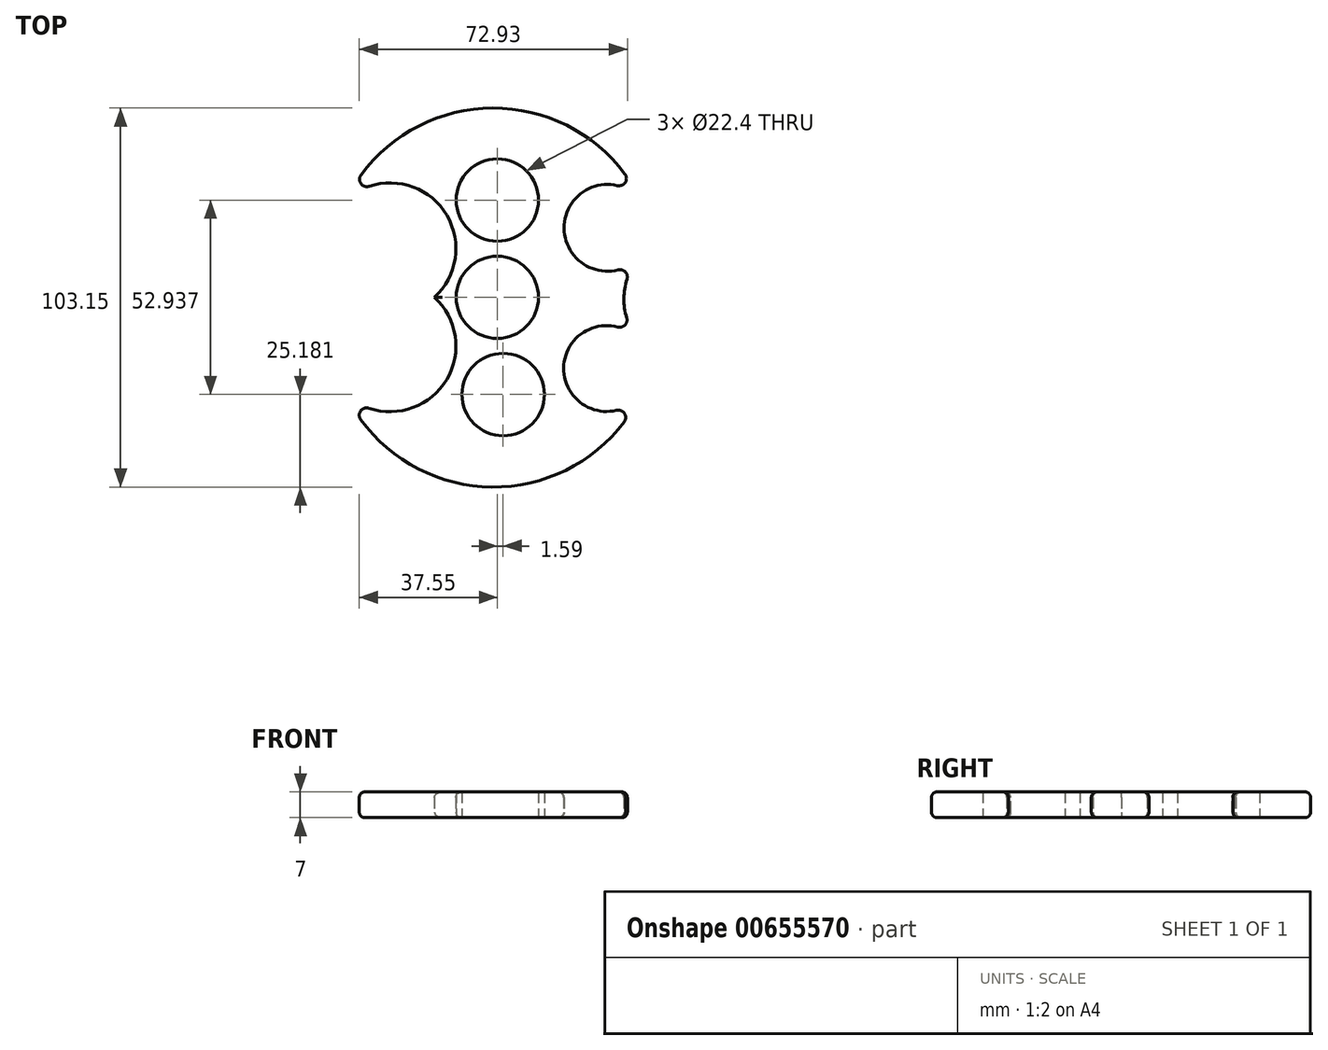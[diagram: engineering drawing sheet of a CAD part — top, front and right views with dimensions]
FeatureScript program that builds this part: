
annotation { "Feature Type Name" : "Feature", "Feature Type Description" : "" }
export const myFeature = defineFeature(function(context is Context, id is Id, definition is map)
    precondition{}
    {
        {
            var Q0;
            Q0=qCreatedBy(makeId("Top.planeOp"),FACE);
            var sketch = newSketch(context, id + "F0", { "sketchPlane" : qUnion([Q0])});
            skCircle(sketch, "E0", {"center": v(0, 0) * mm, "radius": 11.2 * mm});
            skCircle(sketch, "E1", {"center": v(0, 26.47) * mm, "radius": 11.2 * mm});
            skCircle(sketch, "E2.1.1", {"center": v(1.59, -26.47) * mm, "radius": 11.2 * mm});
            skPoint(sketch, "E2.center", {"position": v(0.8, 0) * mm});
            skArc(sketch, "E3", {"start": v(39.06, 26.47) * mm, "mid": v(-1.1, 51.5) * mm, "end": v(-41.24, 26.47) * mm});
            skArc(sketch, "E4", {"start": v(-41.24, -26.47) * mm, "mid": v(-1.1, -51.65) * mm, "end": v(39.06, -26.47) * mm});
            skArc(sketch, "E5", {"start": v(-17.1, 0) * mm, "mid": v(-15.94, 25.3) * mm, "end": v(-41.24, 26.47) * mm});
            skArc(sketch, "E6", {"start": v(-41.24, -26.47) * mm, "mid": v(-15.94, -25.3) * mm, "end": v(-17.1, 0) * mm});
            skLineSegment(sketch, "E7", {"start": v(-17.1, 0) * mm, "end": v(-17.1, 0) * mm});
            skPoint(sketch, "E8.start.orphan", {"position": v(39.06, 6.6) * mm});
            skPoint(sketch, "E9.start.orphan", {"position": v(39.06, -6.3) * mm});
            skArc(sketch, "E10", {"start": v(39.06, 26.47) * mm, "mid": v(18.17, 18.9) * mm, "end": v(39.06, 11.35) * mm});
            skArc(sketch, "E11", {"start": v(39.06, -12.3) * mm, "mid": v(18.05, -19.39) * mm, "end": v(39.06, -26.47) * mm});
            skArc(sketch, "E12", {"start": v(39.06, 11.35) * mm, "mid": v(34.43, -0.48) * mm, "end": v(39.06, -12.3) * mm});
            skSolve(sketch);
        }
        {
            var Q0;
            Q0=makeQuery(id+"F0.imprint","IMPRINT",FACE,{"disambiguationData":[TD([[makeQuery(id+"F0.imprint","IMPRINT",EDGE,{"derivedFrom":sQuery(id+"F0.wireOp",EDGE,"E0")}),-1.0]])]});
            extrude(context, id + "F1", {"entities" : qUnion([Q0]), "depth" : 7 * mm, "offsetDistance" : 25 * mm});
        }
        {
            var Q0;
            Q0=makeQuery(id+"F1.opExtrude","CAP_EDGE",EDGE,{"disambiguationData":[OSD([sQuery(id+"F0.wireOp",EDGE,"E3")])],"isStart":false});
            var Q1;
            Q1=makeQuery(id+"F1.opExtrude","CAP_EDGE",EDGE,{"disambiguationData":[OSD([sQuery(id+"F0.wireOp",EDGE,"E4")])],"isStart":false});
            var Q2;
            Q2=makeQuery(id+"F1.opExtrude","CAP_EDGE",EDGE,{"disambiguationData":[OSD([sQuery(id+"F0.wireOp",EDGE,"E7")])],"isStart":false});
            var Q3;
            Q3=makeQuery(id+"F1.opExtrude","CAP_EDGE",EDGE,{"disambiguationData":[OSD([sQuery(id+"F0.wireOp",EDGE,"E5")])],"isStart":false});
            var Q4;
            Q4=makeQuery(id+"F1.opExtrude","CAP_EDGE",EDGE,{"disambiguationData":[OSD([sQuery(id+"F0.wireOp",EDGE,"E6")])],"isStart":false});
            var Q5;
            Q5=makeQuery(id+"F1.opExtrude","CAP_EDGE",EDGE,{"disambiguationData":[OSD([sQuery(id+"F0.wireOp",EDGE,"E10")])],"isStart":false});
            var Q6;
            Q6=makeQuery(id+"F1.opExtrude","CAP_EDGE",EDGE,{"disambiguationData":[OSD([sQuery(id+"F0.wireOp",EDGE,"E12")])],"isStart":false});
            var Q7;
            Q7=makeQuery(id+"F1.opExtrude","CAP_EDGE",EDGE,{"disambiguationData":[OSD([sQuery(id+"F0.wireOp",EDGE,"E11")])],"isStart":false});
            var Q8;
            Q8=makeQuery(id+"F1.opExtrude","CAP_EDGE",EDGE,{"disambiguationData":[OSD([sQuery(id+"F0.wireOp",EDGE,"E7")])],"isStart":true});
            var Q9;
            Q9=makeQuery(id+"F1.opExtrude","CAP_EDGE",EDGE,{"disambiguationData":[OSD([sQuery(id+"F0.wireOp",EDGE,"E6")])],"isStart":true});
            var Q10;
            Q10=makeQuery(id+"F1.opExtrude","CAP_EDGE",EDGE,{"disambiguationData":[OSD([sQuery(id+"F0.wireOp",EDGE,"E5")])],"isStart":true});
            var Q11;
            Q11=makeQuery(id+"F1.opExtrude","CAP_EDGE",EDGE,{"disambiguationData":[OSD([sQuery(id+"F0.wireOp",EDGE,"E3")])],"isStart":true});
            var Q12;
            Q12=makeQuery(id+"F1.opExtrude","CAP_EDGE",EDGE,{"disambiguationData":[OSD([sQuery(id+"F0.wireOp",EDGE,"E4")])],"isStart":true});
            var Q13;
            Q13=makeQuery(id+"F1.opExtrude","CAP_EDGE",EDGE,{"disambiguationData":[OSD([sQuery(id+"F0.wireOp",EDGE,"E11")])],"isStart":true});
            var Q14;
            Q14=makeQuery(id+"F1.opExtrude","CAP_EDGE",EDGE,{"disambiguationData":[OSD([sQuery(id+"F0.wireOp",EDGE,"E12")])],"isStart":true});
            var Q15;
            Q15=makeQuery(id+"F1.opExtrude","CAP_EDGE",EDGE,{"disambiguationData":[OSD([sQuery(id+"F0.wireOp",EDGE,"E10")])],"isStart":true});
            fillet(context, id + "F2", {"entities" : qUnion([Q0, Q1, Q2, Q3, Q4, Q5, Q6, Q7, Q8, Q9, Q10, Q11, Q12, Q13, Q14, Q15]), "radius" : 1.5 * mm, "tangentPropagation" : true, "allowEdgeOverflow" : false});
        }
        {
            var Q0;
            Q0=makeQuery(id+"F1.opExtrude","SWEPT_EDGE",EDGE,{"disambiguationData":[OSD([sQuery(id+"F0.wireOp",EDGE,"E3"),sQuery(id+"F0.wireOp",EDGE,"E10")])]});
            var Q1;
            Q1=makeQuery(id+"F1.opExtrude","SWEPT_EDGE",EDGE,{"disambiguationData":[OSD([sQuery(id+"F0.wireOp",EDGE,"E10"),sQuery(id+"F0.wireOp",EDGE,"E12")])]});
            var Q2;
            Q2=makeQuery(id+"F1.opExtrude","SWEPT_EDGE",EDGE,{"disambiguationData":[OSD([sQuery(id+"F0.wireOp",EDGE,"E4"),sQuery(id+"F0.wireOp",EDGE,"E11")])]});
            var Q3;
            Q3=makeQuery(id+"F1.opExtrude","SWEPT_EDGE",EDGE,{"disambiguationData":[OSD([sQuery(id+"F0.wireOp",EDGE,"E11"),sQuery(id+"F0.wireOp",EDGE,"E12")])]});
            var Q4;
            Q4=makeQuery(id+"F1.opExtrude","SWEPT_EDGE",EDGE,{"disambiguationData":[OSD([sQuery(id+"F0.wireOp",EDGE,"E3"),sQuery(id+"F0.wireOp",EDGE,"E5")])]});
            var Q5;
            Q5=makeQuery(id+"F1.opExtrude","SWEPT_EDGE",EDGE,{"disambiguationData":[OSD([sQuery(id+"F0.wireOp",EDGE,"E4"),sQuery(id+"F0.wireOp",EDGE,"E6")])]});
            fillet(context, id + "F3", {"entities" : qUnion([Q0, Q1, Q2, Q3, Q4, Q5]), "radius" : 2 * mm, "tangentPropagation" : true, "allowEdgeOverflow" : false});
        }
    });
